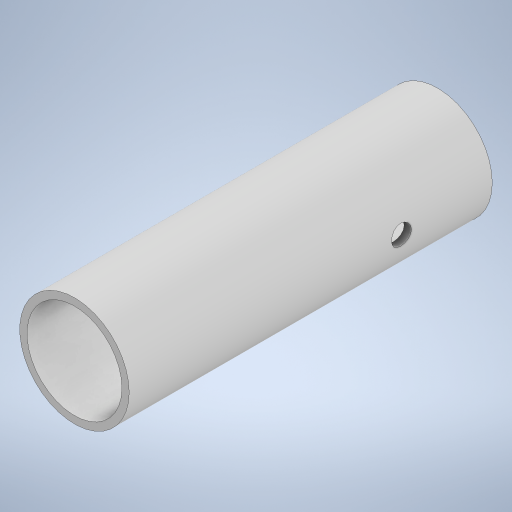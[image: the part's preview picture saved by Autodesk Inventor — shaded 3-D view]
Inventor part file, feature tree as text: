
AUTODESK INVENTOR PART (.ipt)
format: ipt  version: 2024 (Build 280153000, 153)  size: 232,960 bytes
history: native  units: mm
features: extrude x3, sketch x3
ambient origin geometry x8: Origin, YZ Plane, XZ Plane, XY Plane, X Axis, Y Axis, Z Axis, Center Point
bodies: Solid1 (feature_tree)
feature tree (6):
  extrude  "Extrusion1"  Depth=200.0mm TaperAngle=0.0deg
  extrude  "Extrusion2"  Depth=200.0mm TaperAngle=0.0deg
  extrude  "Extrusion3"  Depth=50.0mm
  sketch  "Sketch1"  dims[d0=60.3mm d1=200.0mm d2=0.0mm]
  sketch  "Sketch2"  dims[d3=52.3mm d4=200.0mm d5=0.0mm]
  sketch  "Sketch3"  dims[d6=11.0mm d7=50.0mm d8=0.0mm d9=0.0mm]
